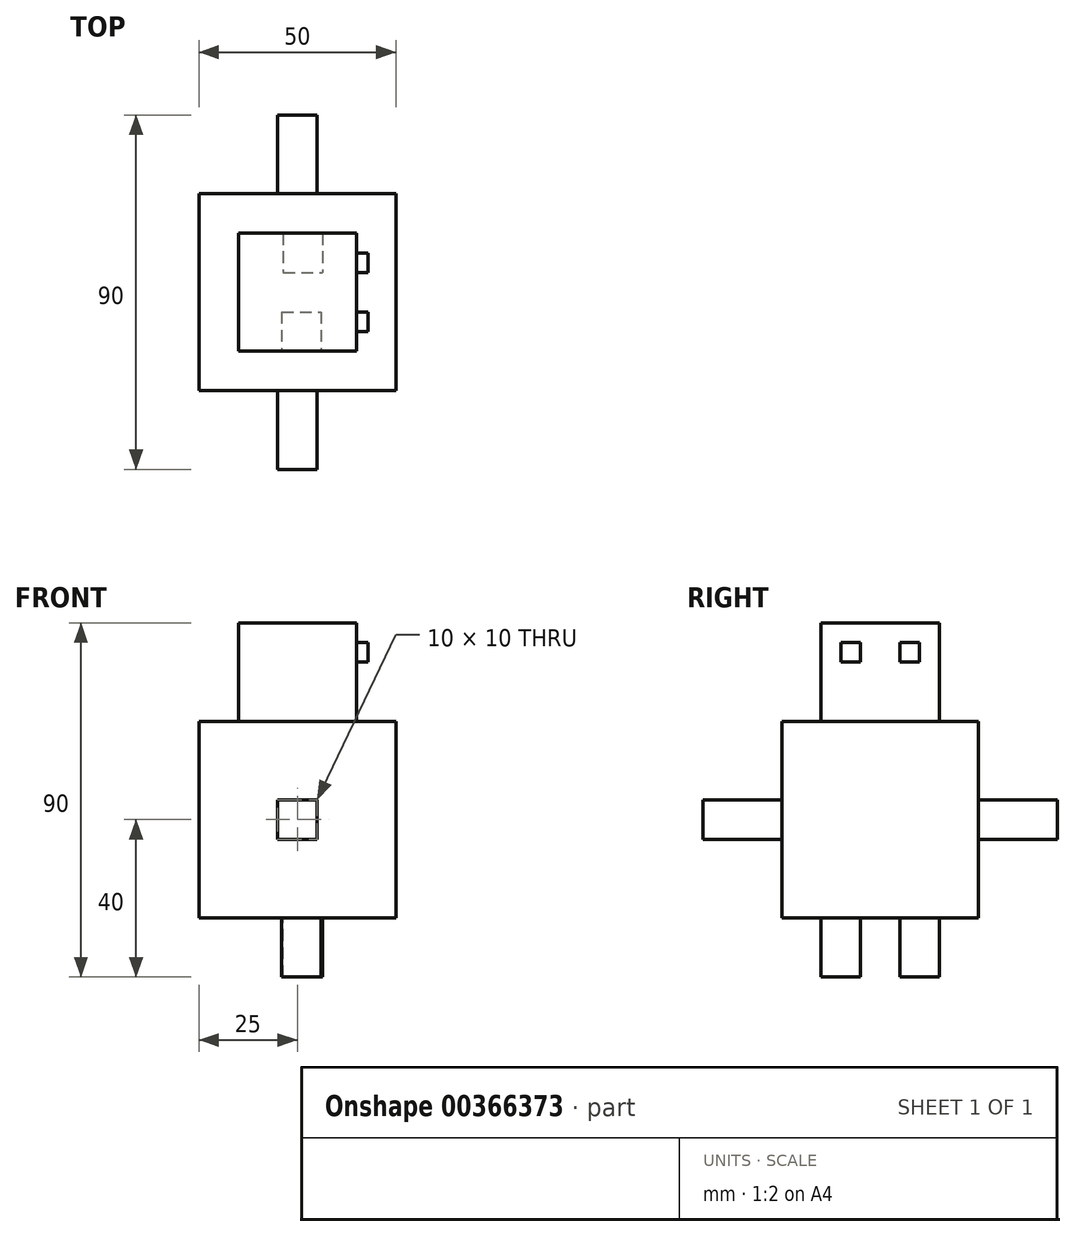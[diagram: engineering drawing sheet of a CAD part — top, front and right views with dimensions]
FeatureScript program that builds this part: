
annotation { "Feature Type Name" : "Feature", "Feature Type Description" : "" }
export const myFeature = defineFeature(function(context is Context, id is Id, definition is map)
    precondition{}
    {
        {
            var Q0;
            Q0=qCreatedBy(makeId("Top.planeOp"),FACE);
            var sketch = newSketch(context, id + "F0", { "sketchPlane" : qUnion([Q0])});
            skLineSegment(sketch, "E0.bottom", {"start": v(0, 0) * mm, "end": v(-50, 0) * mm});
            skLineSegment(sketch, "E0.top", {"start": v(0, 50) * mm, "end": v(-50, 50) * mm});
            skLineSegment(sketch, "E0.left", {"start": v(0, 0) * mm, "end": v(0, 50) * mm});
            skLineSegment(sketch, "E0.right", {"start": v(-50, 0) * mm, "end": v(-50, 50) * mm});
            skSolve(sketch);
        }
        {
            var Q0;
            Q0=makeQuery(id+"F0.imprint","IMPRINT",FACE,{"disambiguationData":[TD([[makeQuery(id+"F0.imprint","IMPRINT",EDGE,{"derivedFrom":sQuery(id+"F0.wireOp",EDGE,"E0.bottom")}),-1.0]])]});
            extrude(context, id + "F1", {"entities" : qUnion([Q0]), "depth" : 50 * mm});
        }
        {
            var Q0;
            Q0=makeQuery(id+"F1.opExtrude","CAP_FACE",FACE,{"disambiguationData":[OSD([sQuery(id+"F0.wireOp",EDGE,"E0.bottom"),sQuery(id+"F0.wireOp",EDGE,"E0.top"),sQuery(id+"F0.wireOp",EDGE,"E0.left"),sQuery(id+"F0.wireOp",EDGE,"E0.right")])],"isStart":false});
            var sketch = newSketch(context, id + "F2", { "sketchPlane" : qUnion([Q0])});
            skLineSegment(sketch, "E1.bottom", {"start": v(-40, 40) * mm, "end": v(-10, 40) * mm});
            skLineSegment(sketch, "E1.top", {"start": v(-40, 10) * mm, "end": v(-10, 10) * mm});
            skLineSegment(sketch, "E1.left", {"start": v(-40, 40) * mm, "end": v(-40, 10) * mm});
            skLineSegment(sketch, "E1.right", {"start": v(-10, 40) * mm, "end": v(-10, 10) * mm});
            skSolve(sketch);
        }
        {
            var Q0;
            Q0=makeQuery(id+"F2.imprint","IMPRINT",FACE,{"disambiguationData":[TD([[makeQuery(id+"F2.imprint","IMPRINT",EDGE,{"derivedFrom":sQuery(id+"F2.wireOp",EDGE,"E1.bottom")}),-1.0]])]});
            extrude(context, id + "F3", {"entities" : qUnion([Q0]), "operationType" : NewBodyOperationType.ADD, "depth" : 25 * mm});
        }
        {
            var Q0;
            Q0=makeQuery(id+"F1.opExtrude","SWEPT_FACE",FACE,{"disambiguationData":[OSD([sQuery(id+"F0.wireOp",EDGE,"E0.bottom")])]});
            var sketch = newSketch(context, id + "F4", { "sketchPlane" : qUnion([Q0])});
            skLineSegment(sketch, "E2.bottom", {"start": v(-30, 30) * mm, "end": v(-20, 30) * mm});
            skLineSegment(sketch, "E2.top", {"start": v(-30, 20) * mm, "end": v(-20, 20) * mm});
            skLineSegment(sketch, "E2.left", {"start": v(-30, 30) * mm, "end": v(-30, 20) * mm});
            skLineSegment(sketch, "E2.right", {"start": v(-20, 30) * mm, "end": v(-20, 20) * mm});
            skSolve(sketch);
        }
        {
            var Q0;
            Q0=makeQuery(id+"F4.imprint","IMPRINT",FACE,{"disambiguationData":[TD([[makeQuery(id+"F4.imprint","IMPRINT",EDGE,{"derivedFrom":sQuery(id+"F4.wireOp",EDGE,"E2.bottom")}),-1.0]])]});
            extrude(context, id + "F5", {"entities" : qUnion([Q0]), "operationType" : NewBodyOperationType.ADD, "depth" : 20 * mm});
        }
        {
            var Q0;
            Q0=makeQuery(id+"F1.opExtrude","SWEPT_FACE",FACE,{"disambiguationData":[OSD([sQuery(id+"F0.wireOp",EDGE,"E0.top")])]});
            var sketch = newSketch(context, id + "F6", { "sketchPlane" : qUnion([Q0])});
            skLineSegment(sketch, "E3.bottom", {"start": v(20, 30) * mm, "end": v(30, 30) * mm});
            skLineSegment(sketch, "E3.top", {"start": v(20, 20) * mm, "end": v(30, 20) * mm});
            skLineSegment(sketch, "E3.left", {"start": v(20, 30) * mm, "end": v(20, 20) * mm});
            skLineSegment(sketch, "E3.right", {"start": v(30, 30) * mm, "end": v(30, 20) * mm});
            skSolve(sketch);
        }
        {
            var Q0;
            Q0=makeQuery(id+"F6.imprint","IMPRINT",FACE,{"disambiguationData":[TD([[makeQuery(id+"F6.imprint","IMPRINT",EDGE,{"derivedFrom":sQuery(id+"F6.wireOp",EDGE,"E3.bottom")}),-1.0]])]});
            extrude(context, id + "F7", {"entities" : qUnion([Q0]), "operationType" : NewBodyOperationType.ADD, "depth" : 20 * mm});
        }
        {
            var Q0;
            Q0=makeQuery(id+"F1.opExtrude","CAP_FACE",FACE,{"disambiguationData":[OSD([sQuery(id+"F0.wireOp",EDGE,"E0.bottom"),sQuery(id+"F0.wireOp",EDGE,"E0.top"),sQuery(id+"F0.wireOp",EDGE,"E0.left"),sQuery(id+"F0.wireOp",EDGE,"E0.right")])],"isStart":true});
            var sketch = newSketch(context, id + "F8", { "sketchPlane" : qUnion([Q0])});
            skLineSegment(sketch, "E4.bottom", {"start": v(-28.6, -40) * mm, "end": v(-18.6, -40) * mm});
            skLineSegment(sketch, "E4.top", {"start": v(-28.6, -30) * mm, "end": v(-18.6, -30) * mm});
            skLineSegment(sketch, "E4.left", {"start": v(-28.6, -40) * mm, "end": v(-28.6, -30) * mm});
            skLineSegment(sketch, "E4.right", {"start": v(-18.6, -40) * mm, "end": v(-18.6, -30) * mm});
            skLineSegment(sketch, "E5.bottom", {"start": v(-28.96, -20) * mm, "end": v(-18.96, -20) * mm});
            skLineSegment(sketch, "E5.top", {"start": v(-28.96, -10) * mm, "end": v(-18.96, -10) * mm});
            skLineSegment(sketch, "E5.left", {"start": v(-28.96, -20) * mm, "end": v(-28.96, -10) * mm});
            skLineSegment(sketch, "E5.right", {"start": v(-18.96, -20) * mm, "end": v(-18.96, -10) * mm});
            skLineSegment(sketch, "E6.left", {"start": v(-28.96, -10) * mm, "end": v(-28.96, -20) * mm});
            skLineSegment(sketch, "E6.right", {"start": v(-18.96, -10) * mm, "end": v(-18.96, -20) * mm});
            skLineSegment(sketch, "E7.left", {"start": v(-28.6, -30) * mm, "end": v(-28.6, -40) * mm});
            skLineSegment(sketch, "E7.right", {"start": v(-18.6, -30) * mm, "end": v(-18.6, -40) * mm});
            skSolve(sketch);
        }
        {
            var Q0;
            Q0 = qSketchRegion(id + "F8", true);
            extrude(context, id + "F9", {"entities" : qUnion([Q0]), "operationType" : NewBodyOperationType.ADD, "depth" : 15 * mm});
        }
        {
            var Q0;
            Q0=makeQuery(id+"F3.opExtrude","SWEPT_FACE",FACE,{"disambiguationData":[OSD([sQuery(id+"F2.wireOp",EDGE,"E1.right")])]});
            var sketch = newSketch(context, id + "F10", { "sketchPlane" : qUnion([Q0])});
            skLineSegment(sketch, "E8.bottom", {"start": v(15, 70) * mm, "end": v(20, 70) * mm});
            skLineSegment(sketch, "E8.top", {"start": v(15, 65) * mm, "end": v(20, 65) * mm});
            skLineSegment(sketch, "E8.left", {"start": v(15, 70) * mm, "end": v(15, 65) * mm});
            skLineSegment(sketch, "E8.right", {"start": v(20, 70) * mm, "end": v(20, 65) * mm});
            skLineSegment(sketch, "E9.bottom", {"start": v(30, 70) * mm, "end": v(35, 70) * mm});
            skLineSegment(sketch, "E9.top", {"start": v(30, 65) * mm, "end": v(35, 65) * mm});
            skLineSegment(sketch, "E9.left", {"start": v(30, 70) * mm, "end": v(30, 65) * mm});
            skLineSegment(sketch, "E9.right", {"start": v(35, 70) * mm, "end": v(35, 65) * mm});
            skSolve(sketch);
        }
        {
            var Q0;
            Q0=makeQuery(id+"F10.imprint","IMPRINT",FACE,{"disambiguationData":[TD([[makeQuery(id+"F10.imprint","IMPRINT",EDGE,{"derivedFrom":sQuery(id+"F10.wireOp",EDGE,"E8.bottom")}),-1.0]])]});
            var Q1;
            Q1=makeQuery(id+"F10.imprint","IMPRINT",FACE,{"disambiguationData":[TD([[makeQuery(id+"F10.imprint","IMPRINT",EDGE,{"derivedFrom":sQuery(id+"F10.wireOp",EDGE,"E9.bottom")}),-1.0]])]});
            extrude(context, id + "F11", {"entities" : qUnion([Q0, Q1]), "operationType" : NewBodyOperationType.ADD, "depth" : 3 * mm});
        }
    });
